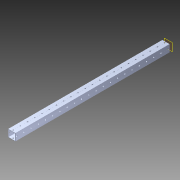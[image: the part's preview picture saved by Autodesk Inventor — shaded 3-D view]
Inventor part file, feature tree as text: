
AUTODESK INVENTOR PART (.ipt)
format: ipt  version: 2014 (Build 180170000, 170)  size: 1,328,128 bytes
history: native  units: in
note: dims shown in document units (in); Inventor stores cm internally (conversion verified against a paired STEP export)
features: extrude x2, sketch x2, pattern_circular x1, other x1, plane x1, imported_body x1, projected_geometry x1
ambient origin geometry x8: Origin, YZ Plane, XZ Plane, XY Plane, X Axis, Y Axis, Z Axis, Center Point
bodies: Body1 (feature_tree)
feature tree (9):
  pattern_circular  "CirPattern2"
  other  "217-3426-STEP1"
  plane  "Work Plane1"
  extrude  "Extrusion1"  Depth=3937.0079in TaperAngle=0.0deg
  extrude  "Extrusion2"  Depth=21.375in
  imported_body  "Base1"
  sketch  "Sketch1"  dims[d0=-22.0in d1=3937.0079in d2=0.0in]
  sketch  "Sketch3"  dims[d3=21.375in d4=11.0in d5=2.0in d6=0.0in]
  projected_geometry  "Projected Loop1"
